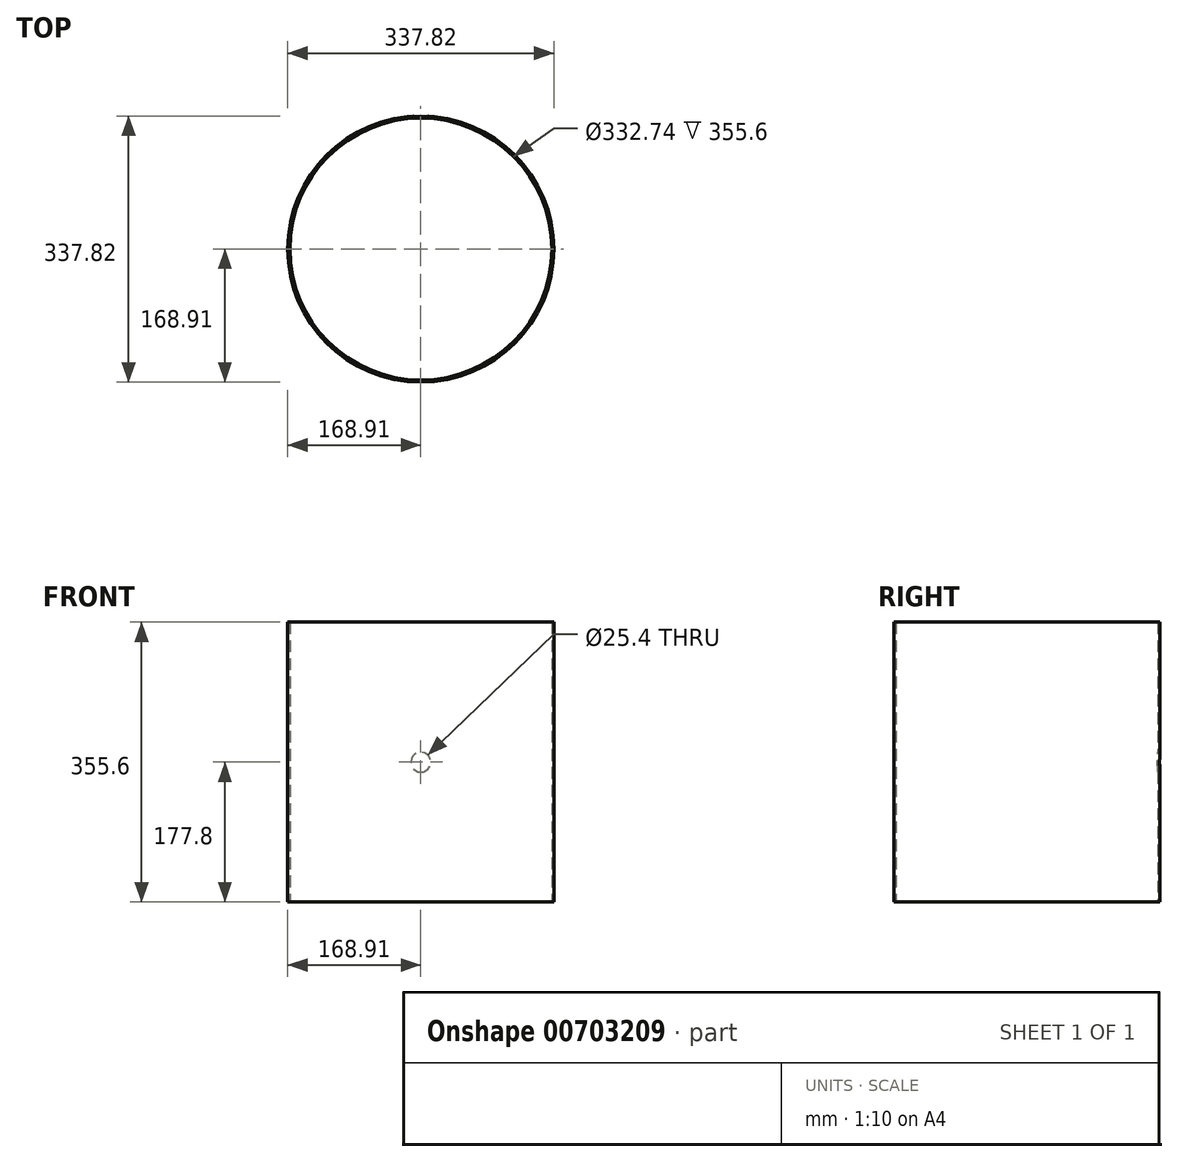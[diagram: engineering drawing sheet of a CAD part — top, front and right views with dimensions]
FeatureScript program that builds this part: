
annotation { "Feature Type Name" : "Feature", "Feature Type Description" : "" }
export const myFeature = defineFeature(function(context is Context, id is Id, definition is map)
    precondition{}
    {
        {
            var Q0;
            Q0=qCreatedBy(makeId("Top.planeOp"),FACE);
            var sketch = newSketch(context, id + "F0", { "sketchPlane" : qUnion([Q0])});
            skCircle(sketch, "E0", {"center": v(0, 0) * mm, "radius": 168.91 * mm});
            skCircle(sketch, "E1", {"center": v(0, 0) * mm, "radius": 166.37 * mm});
            skSolve(sketch);
        }
        {
            var Q0;
            Q0 = qSketchRegion(id + "F0", true);
            extrude(context, id + "F1", {"entities" : qUnion([Q0]), "depth" : 355.6 * mm, "offsetDistance" : 25.4 * mm});
        }
        {
            var Q0;
            Q0=qCreatedBy(makeId("Front.planeOp"),FACE);
            var sketch = newSketch(context, id + "F2", { "sketchPlane" : qUnion([Q0])});
            skCircle(sketch, "E2", {"center": v(0, 177.8) * mm, "radius": 12.7 * mm});
            skSolve(sketch);
        }
        {
            var Q0;
            Q0 = qSketchRegion(id + "F2", true);
            extrude(context, id + "F3", {"entities" : qUnion([Q0]), "operationType" : NewBodyOperationType.REMOVE, "endBound" : BoundingType.THROUGH_ALL, "oppositeDirection" : true, "depth" : 25.4 * mm, "offsetDistance" : 25.4 * mm});
        }
    });
